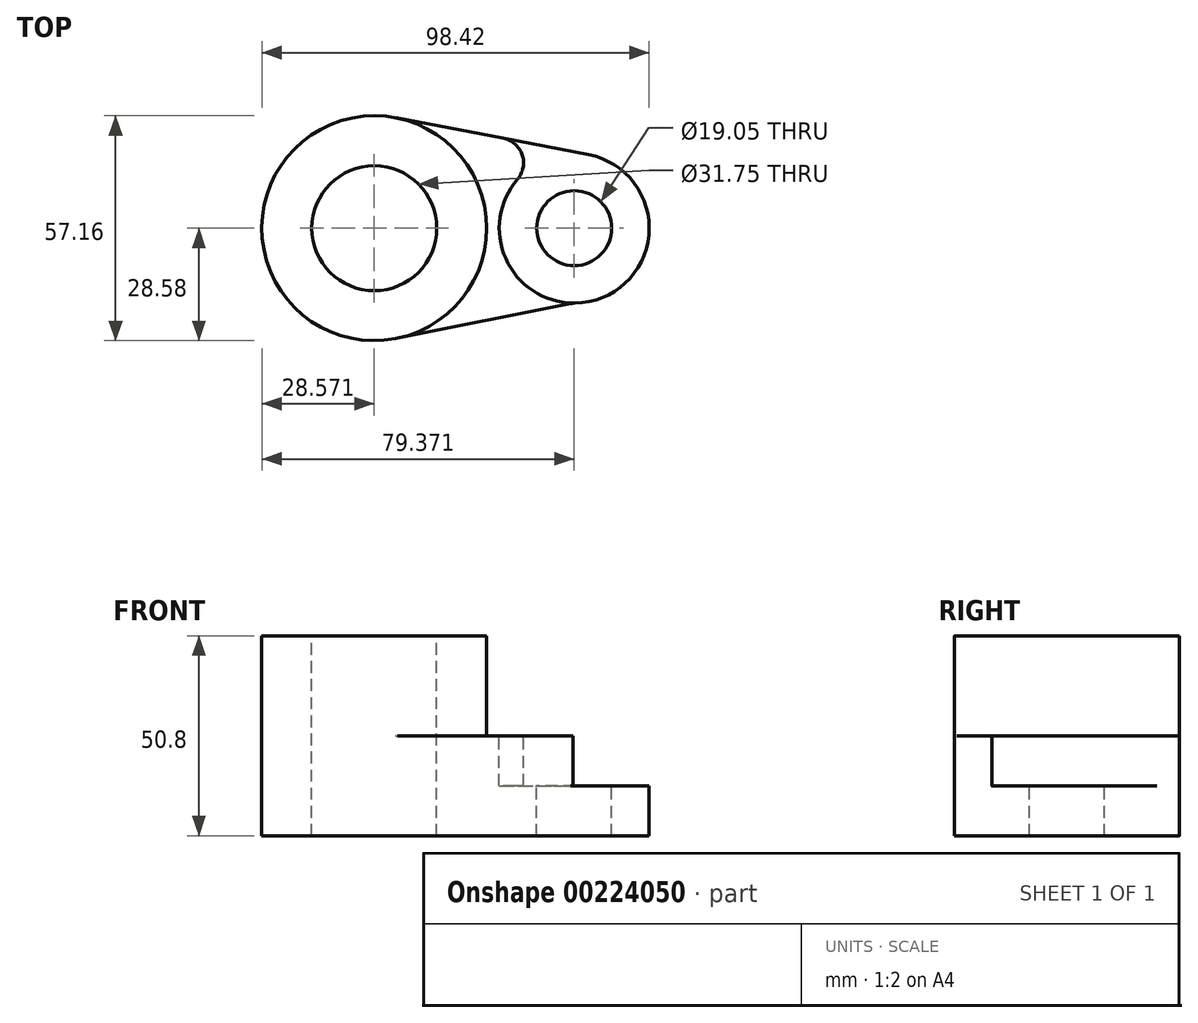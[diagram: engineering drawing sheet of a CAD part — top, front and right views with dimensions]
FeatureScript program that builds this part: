
annotation { "Feature Type Name" : "Feature", "Feature Type Description" : "" }
export const myFeature = defineFeature(function(context is Context, id is Id, definition is map)
    precondition{}
    {
        {
            var Q0;
            Q0=qCreatedBy(makeId("Top.planeOp"),FACE);
            var sketch = newSketch(context, id + "F0", { "sketchPlane" : qUnion([Q0])});
            skCircle(sketch, "E0", {"center": v(-34.8, 0) * mm, "radius": 28.58 * mm});
            skCircle(sketch, "E1", {"center": v(-34.8, 0) * mm, "radius": 15.88 * mm});
            skLineSegment(sketch, "E2", {"start": v(-34.8, 0) * mm, "end": v(16, 0) * mm});
            skCircle(sketch, "E3", {"center": v(16, 0) * mm, "radius": 9.53 * mm});
            skCircle(sketch, "E4", {"center": v(16, 0) * mm, "radius": 19.05 * mm});
            skLineSegment(sketch, "E5", {"start": v(-29.44, 28.07) * mm, "end": v(19.57, 18.71) * mm});
            skLineSegment(sketch, "E6", {"start": v(-29.44, -28.07) * mm, "end": v(15.66, -19.05) * mm});
            skSolve(sketch);
        }
        {
            var Q0;
            Q0 = qSketchRegion(id + "F0", true);
            extrude(context, id + "F1", {"entities" : qUnion([Q0]), "oppositeDirection" : true, "depth" : 25.4 * mm});
        }
        {
            var Q0;
            Q0=makeQuery(id+"F0.imprint","IMPRINT",FACE,{"disambiguationData":[TD([[makeQuery(id+"F0.imprint","IMPRINT",EDGE,{"derivedFrom":sQuery(id+"F0.wireOp",EDGE,"E1")}),-1.0]])]});
            extrude(context, id + "F2", {"entities" : qUnion([Q0]), "operationType" : NewBodyOperationType.ADD, "depth" : 25.4 * mm});
        }
        {
            var Q0;
            Q0=makeQuery(id+"F0.imprint","IMPRINT",FACE,{"disambiguationData":[TD([[makeQuery(id+"F0.imprint","IMPRINT",EDGE,{"derivedFrom":sQuery(id+"F0.wireOp",EDGE,"E3")}),-1.0]])]});
            extrude(context, id + "F3", {"entities" : qUnion([Q0]), "operationType" : NewBodyOperationType.REMOVE, "oppositeDirection" : true, "depth" : 12.7 * mm});
        }
        {
            var Q0;
            {var subQ0=sQuery(id+"F0.wireOp",EDGE,"E6");var subQ1=sQuery(id+"F0.wireOp",EDGE,"E4");Q0=makeQuery(id+"F3.boolean.opBoolean","SPLIT",EDGE,{"disambiguationData":[topologyDisambiguationEdgeConnected([makeQuery(id+"F3.opExtrude","SWEPT_FACE",FACE,{"disambiguationData":[OSD([subQ1])]})])],"derivedFrom":makeQuery(id+"F1.opExtrude","SWEPT_EDGE",EDGE,{"disambiguationData":[OSD([subQ1,subQ0])]})});}
            var Q1;
            {var subQ0=sQuery(id+"F0.wireOp",EDGE,"E5");var subQ1=sQuery(id+"F0.wireOp",EDGE,"E4");Q1=makeQuery(id+"F3.boolean.opBoolean","SPLIT",EDGE,{"disambiguationData":[topologyDisambiguationEdgeConnected([makeQuery(id+"F3.opExtrude","SWEPT_FACE",FACE,{"disambiguationData":[OSD([subQ1])]})])],"derivedFrom":makeQuery(id+"F1.opExtrude","SWEPT_EDGE",EDGE,{"disambiguationData":[OSD([subQ1,subQ0])]})});}
            fillet(context, id + "F4", {"entities" : qUnion([Q0, Q1]), "radius" : 6.35 * mm, "tangentPropagation" : true, "allowEdgeOverflow" : false});
        }
    });
